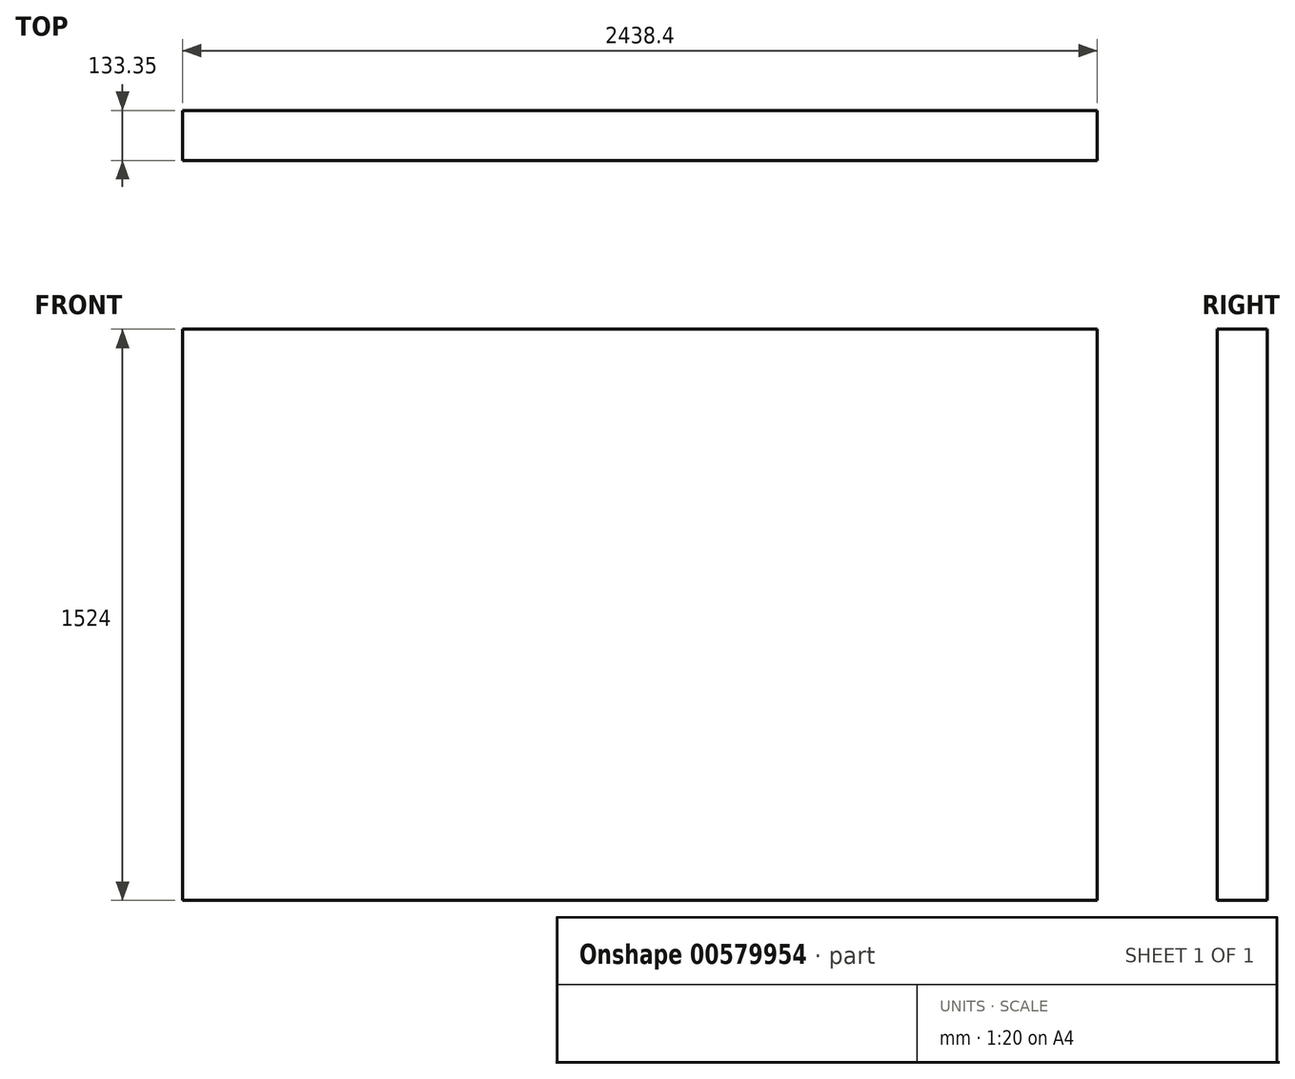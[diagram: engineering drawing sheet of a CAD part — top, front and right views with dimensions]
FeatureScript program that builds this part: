
annotation { "Feature Type Name" : "Feature", "Feature Type Description" : "" }
export const myFeature = defineFeature(function(context is Context, id is Id, definition is map)
    precondition{}
    {
        {
            var Q0;
            Q0=qCreatedBy(makeId("Front.planeOp"),FACE);
            var sketch = newSketch(context, id + "F0", { "sketchPlane" : qUnion([Q0])});
            skLineSegment(sketch, "E0.bottom", {"start": v(-1251.64, 473.75) * mm, "end": v(1186.76, 473.75) * mm});
            skLineSegment(sketch, "E0.top", {"start": v(-1251.64, -1050.25) * mm, "end": v(1186.76, -1050.25) * mm});
            skLineSegment(sketch, "E0.left", {"start": v(-1251.64, 473.75) * mm, "end": v(-1251.64, -1050.25) * mm});
            skLineSegment(sketch, "E0.right", {"start": v(1186.76, 473.75) * mm, "end": v(1186.76, -1050.25) * mm});
            skSolve(sketch);
        }
        {
            var Q0;
            Q0=makeQuery(id+"F0.imprint","IMPRINT",FACE,{"disambiguationData":[TD([[makeQuery(id+"F0.imprint","IMPRINT",EDGE,{"derivedFrom":sQuery(id+"F0.wireOp",EDGE,"E0.bottom")}),-1.0]])]});
            extrude(context, id + "F1", {"entities" : qUnion([Q0]), "depth" : 133.35 * mm, "offsetDistance" : 25.4 * mm});
        }
    });
